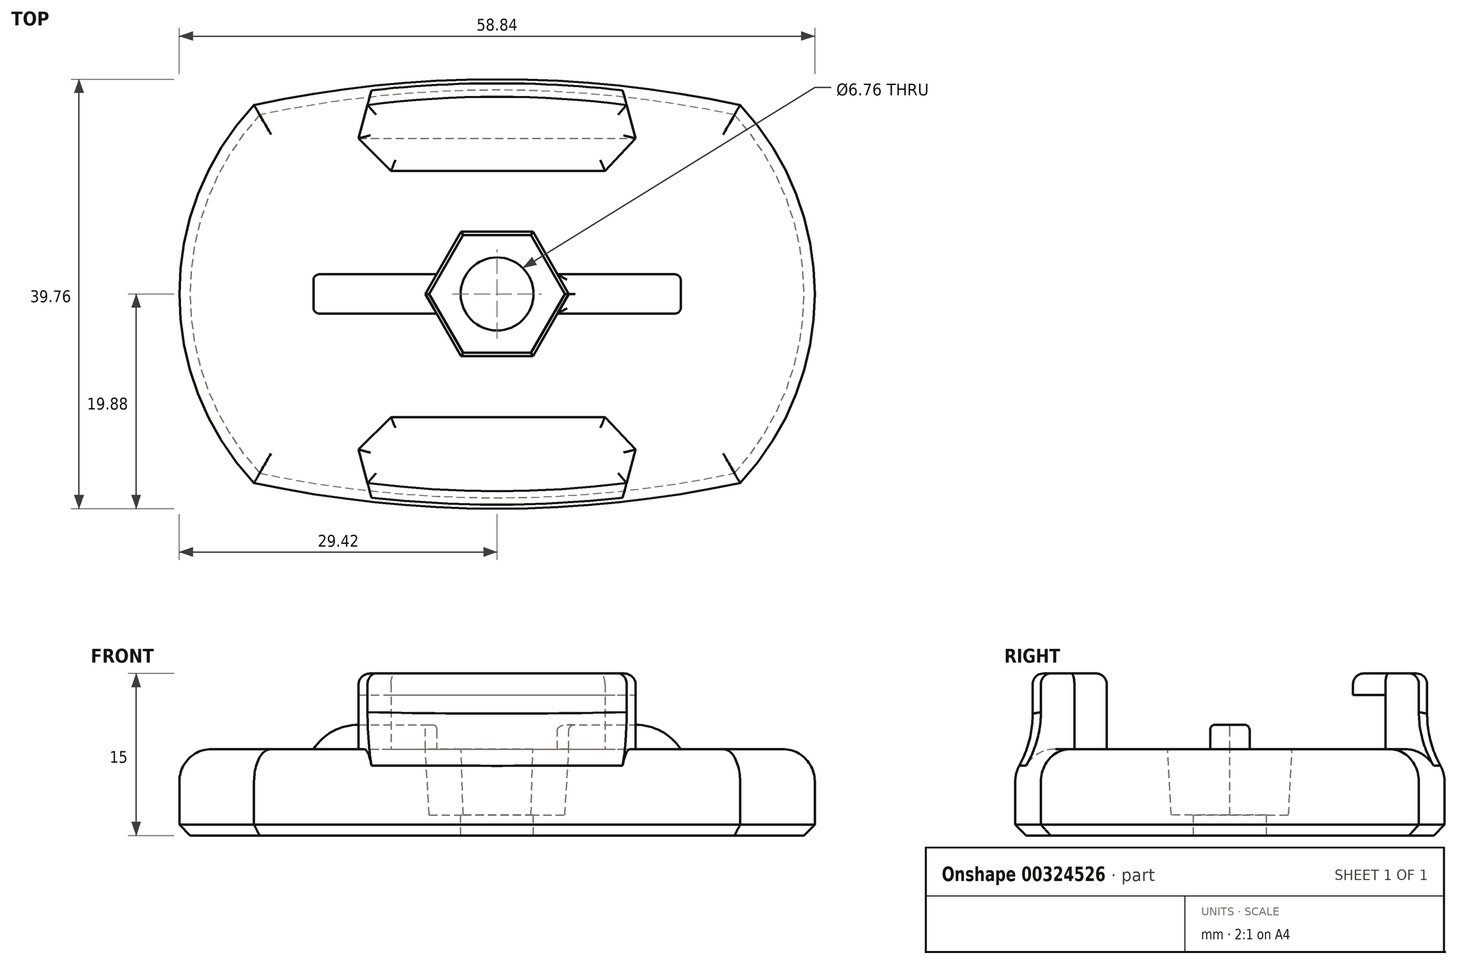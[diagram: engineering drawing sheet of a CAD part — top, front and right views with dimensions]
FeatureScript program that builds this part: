
annotation { "Feature Type Name" : "Feature", "Feature Type Description" : "" }
export const myFeature = defineFeature(function(context is Context, id is Id, definition is map)
    precondition{}
    {
        {
            var Q0;
            Q0=qCreatedBy(makeId("Top.planeOp"),FACE);
            var sketch = newSketch(context, id + "F0", { "sketchPlane" : qUnion([Q0])});
            skLineSegment(sketch, "E0.rect.bottom", {"start": v(-22.5, 17.5) * mm, "end": v(22.5, 17.5) * mm});
            skLineSegment(sketch, "E0.rect.top", {"start": v(-22.5, -17.5) * mm, "end": v(22.5, -17.5) * mm});
            skLineSegment(sketch, "E0.rect.left", {"start": v(-22.5, 17.5) * mm, "end": v(-22.5, -17.5) * mm});
            skLineSegment(sketch, "E0.rect.right", {"start": v(22.5, 17.5) * mm, "end": v(22.5, -17.5) * mm});
            skPoint(sketch, "E0.rect.middle", {"position": v(0, 0) * mm});
            skArc(sketch, "E1", {"start": v(-22.5, 17.5) * mm, "mid": v(-29.42, 0) * mm, "end": v(-22.5, -17.5) * mm});
            skArc(sketch, "E2.MirrorCS", {"start": v(22.5, 17.5) * mm, "mid": v(29.42, 0) * mm, "end": v(22.5, -17.5) * mm});
            skArc(sketch, "E3", {"start": v(22.5, 17.5) * mm, "mid": v(0, 19.88) * mm, "end": v(-22.5, 17.5) * mm});
            skArc(sketch, "E4.MirrorCS", {"start": v(22.5, -17.5) * mm, "mid": v(0, -19.88) * mm, "end": v(-22.5, -17.5) * mm});
            skSolve(sketch);
        }
        {
            var Q0;
            Q0=makeQuery(id+"F0.imprint","IMPRINT",FACE,{"disambiguationData":[TD([[makeQuery(id+"F0.imprint","IMPRINT",EDGE,{"derivedFrom":sQuery(id+"F0.wireOp",EDGE,"E0.rect.bottom")}),-1.0]])]});
            var Q1;
            Q1=makeQuery(id+"F0.imprint","IMPRINT",FACE,{"disambiguationData":[TD([[makeQuery(id+"F0.imprint","IMPRINT",EDGE,{"derivedFrom":sQuery(id+"F0.wireOp",EDGE,"E0.rect.left")}),-1.0]])]});
            var Q2;
            Q2=makeQuery(id+"F0.imprint","IMPRINT",FACE,{"disambiguationData":[TD([[makeQuery(id+"F0.imprint","IMPRINT",EDGE,{"derivedFrom":sQuery(id+"F0.wireOp",EDGE,"E0.rect.right")}),1.0]])]});
            var Q3;
            Q3=makeQuery(id+"F0.imprint","IMPRINT",FACE,{"disambiguationData":[TD([[makeQuery(id+"F0.imprint","IMPRINT",EDGE,{"derivedFrom":sQuery(id+"F0.wireOp",EDGE,"E0.rect.bottom")}),1.0]])]});
            var Q4;
            Q4=makeQuery(id+"F0.imprint","IMPRINT",FACE,{"disambiguationData":[TD([[makeQuery(id+"F0.imprint","IMPRINT",EDGE,{"derivedFrom":sQuery(id+"F0.wireOp",EDGE,"E0.rect.top")}),-1.0]])]});
            extrude(context, id + "F1", {"entities" : qUnion([Q0, Q1, Q2, Q3, Q4]), "depth" : 8 * mm});
        }
        {
            var Q0;
            Q0=makeQuery(id+"F1.opExtrude","CAP_FACE",FACE,{"disambiguationData":[OSD([sQuery(id+"F0.wireOp",EDGE,"E1"),sQuery(id+"F0.wireOp",EDGE,"E2.MirrorCS"),sQuery(id+"F0.wireOp",EDGE,"E3"),sQuery(id+"F0.wireOp",EDGE,"E4.MirrorCS")])],"isStart":false});
            var sketch = newSketch(context, id + "F2", { "sketchPlane" : qUnion([Q0])});
            skLineSegment(sketch, "E5.rect.bottom", {"start": v(-17, 1.82) * mm, "end": v(17, 1.82) * mm});
            skLineSegment(sketch, "E5.rect.top", {"start": v(-17, -1.83) * mm, "end": v(17, -1.83) * mm});
            skLineSegment(sketch, "E5.rect.left", {"start": v(-17, 1.82) * mm, "end": v(-17, -1.83) * mm});
            skLineSegment(sketch, "E5.rect.right", {"start": v(17, 1.82) * mm, "end": v(17, -1.83) * mm});
            skPoint(sketch, "E5.rect.middle", {"position": v(0, 0) * mm});
            skSolve(sketch);
        }
        {
            var Q0;
            Q0=makeQuery(id+"F2.imprint","IMPRINT",FACE,{"disambiguationData":[TD([[makeQuery(id+"F2.imprint","IMPRINT",EDGE,{"derivedFrom":sQuery(id+"F2.wireOp",EDGE,"E5.rect.bottom")}),-1.0]])]});
            extrude(context, id + "F3", {"entities" : qUnion([Q0]), "operationType" : NewBodyOperationType.ADD, "depth" : 2.25 * mm});
        }
        {
            var Q0;
            Q0=makeQuery(id+"F3.opExtrude","SWEPT_FACE",FACE,{"disambiguationData":[OSD([sQuery(id+"F2.wireOp",EDGE,"E5.rect.top")])]});
            var sketch = newSketch(context, id + "F4", { "sketchPlane" : qUnion([Q0])});
            skLineSegment(sketch, "E6", {"start": v(-17, 10.25) * mm, "end": v(17, 10.25) * mm, "construction": true});
            skLineSegment(sketch, "E7.0", {"start": v(-17, 9.25) * mm, "end": v(17, 9.25) * mm});
            skArc(sketch, "E8", {"start": v(-13.26, 10.25) * mm, "mid": v(-15.2, 10) * mm, "end": v(-17, 9.25) * mm});
            skLineSegment(sketch, "E9", {"start": v(0, 0) * mm, "end": v(0, 15.47) * mm, "construction": true});
            skArc(sketch, "E10.0.MirrorCS", {"start": v(13.26, 10.25) * mm, "mid": v(15.2, 10) * mm, "end": v(17, 9.25) * mm});
            skLineSegment(sketch, "E11", {"start": v(-17, 9.25) * mm, "end": v(-18.16, 9.25) * mm});
            skLineSegment(sketch, "E12", {"start": v(-18.16, 9.25) * mm, "end": v(-18.16, 11.7) * mm});
            skLineSegment(sketch, "E13", {"start": v(-18.16, 11.7) * mm, "end": v(-13.25, 11.7) * mm});
            skLineSegment(sketch, "E14", {"start": v(-13.25, 11.7) * mm, "end": v(-13.26, 10.25) * mm});
            skLineSegment(sketch, "E15", {"start": v(13.26, 10.25) * mm, "end": v(13.26, 11.4) * mm});
            skLineSegment(sketch, "E16", {"start": v(13.26, 11.4) * mm, "end": v(18.11, 11.4) * mm});
            skLineSegment(sketch, "E17", {"start": v(18.11, 11.4) * mm, "end": v(18.11, 9.28) * mm});
            skLineSegment(sketch, "E18", {"start": v(18.11, 9.28) * mm, "end": v(17, 9.25) * mm});
            skSolve(sketch);
        }
        {
            var Q0;
            Q0=makeQuery(id+"F1.opExtrude","CAP_FACE",FACE,{"disambiguationData":[OSD([sQuery(id+"F0.wireOp",EDGE,"E1"),sQuery(id+"F0.wireOp",EDGE,"E2.MirrorCS"),sQuery(id+"F0.wireOp",EDGE,"E3"),sQuery(id+"F0.wireOp",EDGE,"E4.MirrorCS")])],"isStart":false});
            var sketch = newSketch(context, id + "F5", { "sketchPlane" : qUnion([Q0])});
            skLineSegment(sketch, "E19.rect.bottom", {"start": v(-12, 17.5) * mm, "end": v(12, 17.5) * mm, "construction": true});
            skPoint(sketch, "E19.rect.middle", {"position": v(0, 0) * mm});
            skLineSegment(sketch, "E20.0", {"start": v(-9.82, 11.4) * mm, "end": v(10, 11.4) * mm});
            skLineSegment(sketch, "E21", {"start": v(-9.82, 11.4) * mm, "end": v(-12.82, 14.4) * mm, "construction": true});
            skLineSegment(sketch, "E22", {"start": v(-9.82, 11.4) * mm, "end": v(-12.83, 14.4) * mm, "construction": true});
            skLineSegment(sketch, "E23.0.MirrorCS", {"start": v(10, 11.4) * mm, "end": v(12.82, 14.4) * mm, "construction": true});
            skLineSegment(sketch, "E24", {"start": v(10, 11.4) * mm, "end": v(12.82, 14.4) * mm});
            skLineSegment(sketch, "E25", {"start": v(12, 17.5) * mm, "end": v(-12, 17.5) * mm});
            skLineSegment(sketch, "E26", {"start": v(-12.83, 14.4) * mm, "end": v(-9.82, 11.4) * mm});
            skLineSegment(sketch, "E27", {"start": v(12.83, 14.4) * mm, "end": v(12, 17.5) * mm});
            skLineSegment(sketch, "E28.0.MirrorCS", {"start": v(-12.83, 14.4) * mm, "end": v(-12, 17.5) * mm});
            skArc(sketch, "E29", {"start": v(12, 17.5) * mm, "mid": v(0, 18.26) * mm, "end": v(-12, 17.5) * mm});
            skLineSegment(sketch, "E30.MirrorCS", {"start": v(12, -17.5) * mm, "end": v(-12, -17.5) * mm});
            skLineSegment(sketch, "E31.MirrorCS", {"start": v(-12.83, -14.4) * mm, "end": v(-9.82, -11.4) * mm});
            skLineSegment(sketch, "E32.MirrorCS", {"start": v(-9.82, -11.4) * mm, "end": v(-12.82, -14.4) * mm, "construction": true});
            skLineSegment(sketch, "E33.MirrorCS", {"start": v(10, -11.4) * mm, "end": v(12.82, -14.4) * mm});
            skLineSegment(sketch, "E34.MirrorCS", {"start": v(-12, -17.5) * mm, "end": v(12, -17.5) * mm, "construction": true});
            skLineSegment(sketch, "E35.MirrorCS", {"start": v(-9.82, -11.4) * mm, "end": v(-12.83, -14.4) * mm, "construction": true});
            skLineSegment(sketch, "E36.MirrorCS", {"start": v(10, -11.4) * mm, "end": v(12.82, -14.4) * mm, "construction": true});
            skLineSegment(sketch, "E37.MirrorCS", {"start": v(-12.83, -14.4) * mm, "end": v(-12, -17.5) * mm});
            skLineSegment(sketch, "E38.MirrorCS", {"start": v(12.83, -14.4) * mm, "end": v(12, -17.5) * mm});
            skLineSegment(sketch, "E39.MirrorCS", {"start": v(-9.82, -11.4) * mm, "end": v(10, -11.4) * mm});
            skArc(sketch, "E40.MirrorCS", {"start": v(12, -17.5) * mm, "mid": v(0, -18.26) * mm, "end": v(-12, -17.5) * mm});
            skSolve(sketch);
        }
        {
            var Q0;
            Q0 = qSketchRegion(id + "F5", true);
            extrude(context, id + "F6", {"entities" : qUnion([Q0]), "operationType" : NewBodyOperationType.ADD, "depth" : 7 * mm});
        }
        {
            var Q0;
            Q0=qCreatedBy(makeId("Right.planeOp"),FACE);
            var sketch = newSketch(context, id + "F7", { "sketchPlane" : qUnion([Q0])});
            skLineSegment(sketch, "E41.0", {"start": v(14.4, 13) * mm, "end": v(14.4, 8) * mm});
            skLineSegment(sketch, "E42.bottom", {"start": v(14.4, 8) * mm, "end": v(10.15, 8) * mm});
            skLineSegment(sketch, "E42.top", {"start": v(14.4, 13) * mm, "end": v(10.15, 13) * mm});
            skLineSegment(sketch, "E42.left", {"start": v(14.4, 8) * mm, "end": v(14.4, 13) * mm});
            skLineSegment(sketch, "E42.right", {"start": v(10.15, 8) * mm, "end": v(10.15, 13) * mm});
            skLineSegment(sketch, "E43.0.MirrorCS", {"start": v(-14.4, 8) * mm, "end": v(-14.4, 13) * mm});
            skLineSegment(sketch, "E43.1.MirrorCS", {"start": v(-14.4, 13) * mm, "end": v(-14.4, 8) * mm});
            skLineSegment(sketch, "E43.2.MirrorCS", {"start": v(-14.4, 13) * mm, "end": v(-10.15, 13) * mm});
            skLineSegment(sketch, "E43.3.MirrorCS", {"start": v(-10.15, 8) * mm, "end": v(-10.15, 13) * mm});
            skLineSegment(sketch, "E43.4.MirrorCS", {"start": v(-14.4, 8) * mm, "end": v(-10.15, 8) * mm});
            skSolve(sketch);
        }
        {
            var Q0;
            Q0=makeQuery(id+"F7.imprint","IMPRINT",FACE,{"disambiguationData":[TD([[makeQuery(id+"F7.imprint","IMPRINT",EDGE,{"derivedFrom":sQuery(id+"F7.wireOp",EDGE,"E42.bottom")}),-1.0]])]});
            var Q1;
            Q1=makeQuery(id+"F7.imprint","IMPRINT",FACE,{"disambiguationData":[TD([[makeQuery(id+"F7.imprint","IMPRINT",EDGE,{"derivedFrom":sQuery(id+"F7.wireOp",EDGE,"E43.1.MirrorCS")}),1.0]])]});
            extrude(context, id + "F8", {"entities" : qUnion([Q0, Q1]), "operationType" : NewBodyOperationType.REMOVE, "endBound" : BoundingType.SYMMETRIC, "oppositeDirection" : true, "depth" : 31.01 * mm});
        }
        {
            var Q0;
            Q0=makeQuery(id+"F1.opExtrude","CAP_EDGE",EDGE,{"disambiguationData":[OSD([sQuery(id+"F0.wireOp",EDGE,"E3")])],"isStart":false});
            var Q1;
            Q1=makeQuery(id+"F1.opExtrude","CAP_EDGE",EDGE,{"disambiguationData":[OSD([sQuery(id+"F0.wireOp",EDGE,"E1")])],"isStart":false});
            var Q2;
            Q2=makeQuery(id+"F1.opExtrude","CAP_EDGE",EDGE,{"disambiguationData":[OSD([sQuery(id+"F0.wireOp",EDGE,"E4.MirrorCS")])],"isStart":false});
            var Q3;
            Q3=makeQuery(id+"F1.opExtrude","CAP_EDGE",EDGE,{"disambiguationData":[OSD([sQuery(id+"F0.wireOp",EDGE,"E2.MirrorCS")])],"isStart":false});
            fillet(context, id + "F9", {"entities" : qUnion([Q0, Q1, Q2, Q3]), "radius" : 3 * mm, "tangentPropagation" : true, "allowEdgeOverflow" : false});
        }
        {
            var Q0;
            Q0=makeQuery(id+"F9.opFillet","BLEND_EDGE",EDGE,{"blendedFrom":[makeQuery(id+"F1.opExtrude","CAP_EDGE",EDGE,{"disambiguationData":[OSD([sQuery(id+"F0.wireOp",EDGE,"E4.MirrorCS")])],"isStart":false}),makeQuery(id+"F6.opExtrude","SWEPT_FACE",FACE,{"disambiguationData":[OSD([sQuery(id+"F5.wireOp",EDGE,"E40.MirrorCS")])]})],"blendedInto":[makeQuery(id+"F6.opExtrude","SWEPT_FACE",FACE,{"disambiguationData":[OSD([sQuery(id+"F5.wireOp",EDGE,"E40.MirrorCS")])]})]});
            var Q1;
            Q1=makeQuery(id+"F9.opFillet","BLEND_EDGE",EDGE,{"blendedFrom":[makeQuery(id+"F1.opExtrude","CAP_EDGE",EDGE,{"disambiguationData":[OSD([sQuery(id+"F0.wireOp",EDGE,"E3")])],"isStart":false}),makeQuery(id+"F6.opExtrude","SWEPT_FACE",FACE,{"disambiguationData":[OSD([sQuery(id+"F5.wireOp",EDGE,"E29")])]})],"blendedInto":[makeQuery(id+"F6.opExtrude","SWEPT_FACE",FACE,{"disambiguationData":[OSD([sQuery(id+"F5.wireOp",EDGE,"E29")])]})]});
            fillet(context, id + "F10", {"entities" : qUnion([Q0, Q1]), "radius" : 10 * mm, "tangentPropagation" : true, "allowEdgeOverflow" : false});
        }
        {
            var Q0;
            Q0=makeQuery(id+"F6.opExtrude","CAP_FACE",FACE,{"disambiguationData":[OSD([sQuery(id+"F5.wireOp",EDGE,"E31.MirrorCS"),sQuery(id+"F5.wireOp",EDGE,"E33.MirrorCS"),sQuery(id+"F5.wireOp",EDGE,"E37.MirrorCS"),sQuery(id+"F5.wireOp",EDGE,"E38.MirrorCS"),sQuery(id+"F5.wireOp",EDGE,"E39.MirrorCS"),sQuery(id+"F5.wireOp",EDGE,"E40.MirrorCS")])],"isStart":false});
            var Q1;
            Q1=makeQuery(id+"F6.opExtrude","CAP_FACE",FACE,{"disambiguationData":[OSD([sQuery(id+"F5.wireOp",EDGE,"E20.0"),sQuery(id+"F5.wireOp",EDGE,"E24"),sQuery(id+"F5.wireOp",EDGE,"E26"),sQuery(id+"F5.wireOp",EDGE,"E27"),sQuery(id+"F5.wireOp",EDGE,"E28.0.MirrorCS"),sQuery(id+"F5.wireOp",EDGE,"E29")])],"isStart":false});
            fillet(context, id + "F11", {"entities" : qUnion([Q0, Q1]), "radius" : 1 * mm, "tangentPropagation" : true, "allowEdgeOverflow" : false});
        }
        {
            var Q0;
            Q0=makeQuery(id+"F8.boolean.opBoolean","MERGE",FACE,{"derivedFrom":[makeQuery(id+"F1.opExtrude","CAP_FACE",FACE,{"disambiguationData":[OSD([sQuery(id+"F0.wireOp",EDGE,"E0.rect.bottom"),sQuery(id+"F0.wireOp",EDGE,"E0.rect.top"),sQuery(id+"F0.wireOp",EDGE,"E1"),sQuery(id+"F0.wireOp",EDGE,"E2.MirrorCS")])],"isStart":false}),makeQuery(id+"F8.opExtrude","SWEPT_FACE",FACE,{"disambiguationData":[OSD([sQuery(id+"F7.wireOp",EDGE,"E42.bottom")])]}),makeQuery(id+"F8.opExtrude","SWEPT_FACE",FACE,{"disambiguationData":[OSD([sQuery(id+"F7.wireOp",EDGE,"E43.4.MirrorCS")])]})]});
            var sketch = newSketch(context, id + "F12", { "sketchPlane" : qUnion([Q0])});
            skCircle(sketch, "E44.cCircle", {"center": v(0, 0) * mm, "radius": 5.76 * mm, "construction": true});
            skLineSegment(sketch, "E44.0", {"start": v(-3.32, -5.76) * mm, "end": v(-6.65, 0) * mm});
            skLineSegment(sketch, "E44.1", {"start": v(-6.65, 0) * mm, "end": v(-3.32, 5.76) * mm});
            skLineSegment(sketch, "E44.2", {"start": v(-3.32, 5.76) * mm, "end": v(3.32, 5.76) * mm});
            skLineSegment(sketch, "E44.3", {"start": v(3.32, 5.76) * mm, "end": v(6.65, 0) * mm});
            skLineSegment(sketch, "E44.4", {"start": v(6.65, 0) * mm, "end": v(3.32, -5.76) * mm});
            skLineSegment(sketch, "E44.5", {"start": v(3.32, -5.76) * mm, "end": v(-3.32, -5.76) * mm});
            skPoint(sketch, "E44.0.midPoint", {"position": v(-4.99, -2.88) * mm});
            skSolve(sketch);
        }
        {
            var Q0;
            Q0 = qSketchRegion(id + "F12", true);
            var Q1;
            Q1=makeQuery(id+"F3.opExtrude","CAP_FACE",FACE,{"disambiguationData":[OSD([sQuery(id+"F2.wireOp",EDGE,"E5.rect.bottom"),sQuery(id+"F2.wireOp",EDGE,"E5.rect.top"),sQuery(id+"F2.wireOp",EDGE,"E5.rect.left"),sQuery(id+"F2.wireOp",EDGE,"E5.rect.right")])],"isStart":false});
            extrude(context, id + "F13", {"entities" : qUnion([Q0]), "operationType" : NewBodyOperationType.REMOVE, "oppositeDirection" : true, "depth" : (7 / 32) * 27.94 * mm, "hasDraft" : true, "draftAngle" : 3 * degree, "draftPullDirection" : true, "hasSecondDirection" : true, "secondDirectionBound" : SecondDirectionBoundingType.UP_TO_SURFACE, "secondDirectionOppositeDirection" : false, "secondDirectionBoundEntityFace" : qUnion([Q1]), "secondDirectionDepth" : 25 * mm});
        }
        {
            var Q0;
            Q0=sQuery(id+"F12.wireOp",VERTEX,"E44.cCircle.center");
            var Q1;
            Q1=makeQuery(id+"F1.opExtrude","SWEPT_BODY",BODY,{"disambiguationData":[OSD([sQuery(id+"F0.wireOp",EDGE,"E0.rect.bottom"),sQuery(id+"F0.wireOp",EDGE,"E0.rect.top"),sQuery(id+"F0.wireOp",EDGE,"E1"),sQuery(id+"F0.wireOp",EDGE,"E2.MirrorCS")])]});
            hole(context, id + "F14", {"style" : HoleStyle.SIMPLE, "endStyle" : HoleEndStyle.THROUGH, "standardTappedOrClearance" : lookupTablePath({ "standard" : "ANSI", "fit" : "Normal (ASME)", "size" : "1/4", "type" : "Clearance" }), "standardBlindInLast" : lookupTablePath({ "fit" : "Free", "standard" : "ANSI", "size" : "1/4", "type" : "Clearance" }), "holeDiameter" : 6.76 * mm, "tappedDepth" : 12 * mm, "tapClearance" : 3, "locations" : qUnion([Q0]), "scope" : qUnion([Q1])});
        }
        {
            var Q0;
            Q0=makeQuery(id+"F1.opExtrude","CAP_EDGE",EDGE,{"disambiguationData":[OSD([sQuery(id+"F0.wireOp",EDGE,"E0.rect.top")])],"isStart":true});
            var Q1;
            Q1=makeQuery(id+"F1.opExtrude","CAP_EDGE",EDGE,{"disambiguationData":[OSD([sQuery(id+"F0.wireOp",EDGE,"E2.MirrorCS")])],"isStart":true});
            var Q2;
            Q2=makeQuery(id+"F1.opExtrude","CAP_EDGE",EDGE,{"disambiguationData":[OSD([sQuery(id+"F0.wireOp",EDGE,"E0.rect.bottom")])],"isStart":true});
            var Q3;
            Q3=makeQuery(id+"F1.opExtrude","CAP_EDGE",EDGE,{"disambiguationData":[OSD([sQuery(id+"F0.wireOp",EDGE,"E1")])],"isStart":true});
            var Q4;
            Q4=makeQuery(id+"F1.opExtrude","CAP_EDGE",EDGE,{"disambiguationData":[OSD([sQuery(id+"F0.wireOp",EDGE,"E3")])],"isStart":true});
            var Q5;
            Q5=makeQuery(id+"F1.opExtrude","CAP_EDGE",EDGE,{"disambiguationData":[OSD([sQuery(id+"F0.wireOp",EDGE,"E4.MirrorCS")])],"isStart":true});
            chamfer(context, id + "F15", {"entities" : qUnion([Q0, Q1, Q2, Q3, Q4, Q5]), "width" : 1 * mm, "tangentPropagation" : true});
        }
        {
            var Q0;
            Q0=makeQuery(id+"F3.opExtrude","CAP_EDGE",EDGE,{"disambiguationData":[OSD([sQuery(id+"F2.wireOp",EDGE,"E5.rect.right")])],"isStart":false});
            var Q1;
            Q1=makeQuery(id+"F3.opExtrude","CAP_EDGE",EDGE,{"disambiguationData":[OSD([sQuery(id+"F2.wireOp",EDGE,"E5.rect.left")])],"isStart":false});
            fillet(context, id + "F16", {"entities" : qUnion([Q0, Q1]), "radius" : 5 * mm, "tangentPropagation" : true, "allowEdgeOverflow" : false});
        }
        {
            var Q0;
            {var subQ0=sQuery(id+"F2.wireOp",EDGE,"E5.rect.right");var subQ1=sQuery(id+"F2.wireOp",EDGE,"E5.rect.top");Q0=makeQuery(id+"F13.boolean.opBoolean","SPLIT",EDGE,{"disambiguationData":[TD([makeQuery(id+"F3.opExtrude","SWEPT_FACE",FACE,{"disambiguationData":[OSD([subQ0])]})])],"derivedFrom":makeQuery(id+"F3.opExtrude","CAP_EDGE",EDGE,{"disambiguationData":[OSD([subQ1])],"isStart":false})});}
            var Q1;
            {var subQ0=sQuery(id+"F2.wireOp",EDGE,"E5.rect.bottom");var subQ1=sQuery(id+"F2.wireOp",EDGE,"E5.rect.right");Q1=makeQuery(id+"F13.boolean.opBoolean","SPLIT",EDGE,{"disambiguationData":[TD([makeQuery(id+"F3.opExtrude","SWEPT_FACE",FACE,{"disambiguationData":[OSD([subQ1])]})])],"derivedFrom":makeQuery(id+"F3.opExtrude","CAP_EDGE",EDGE,{"disambiguationData":[OSD([subQ0])],"isStart":false})});}
            var Q2;
            {var subQ0=sQuery(id+"F2.wireOp",EDGE,"E5.rect.bottom");var subQ1=sQuery(id+"F2.wireOp",EDGE,"E5.rect.left");Q2=makeQuery(id+"F13.boolean.opBoolean","SPLIT",EDGE,{"disambiguationData":[TD([makeQuery(id+"F3.opExtrude","SWEPT_FACE",FACE,{"disambiguationData":[OSD([subQ1])]})])],"derivedFrom":makeQuery(id+"F3.opExtrude","CAP_EDGE",EDGE,{"disambiguationData":[OSD([subQ0])],"isStart":false})});}
            var Q3;
            {var subQ0=sQuery(id+"F2.wireOp",EDGE,"E5.rect.left");var subQ1=sQuery(id+"F2.wireOp",EDGE,"E5.rect.top");Q3=makeQuery(id+"F13.boolean.opBoolean","SPLIT",EDGE,{"disambiguationData":[TD([makeQuery(id+"F3.opExtrude","SWEPT_FACE",FACE,{"disambiguationData":[OSD([subQ0])]})])],"derivedFrom":makeQuery(id+"F3.opExtrude","CAP_EDGE",EDGE,{"disambiguationData":[OSD([subQ1])],"isStart":false})});}
            var Q4;
            Q4=makeQuery(id+"F13.boolean.opBoolean","COPY",EDGE,{"derivedFrom":makeQuery(id+"F13.opExtrude","CAP_EDGE",EDGE,{"disambiguationData":[OSD([sQuery(id+"F12.wireOp",EDGE,"E44.1")])],"isStart":true})});
            var Q5;
            Q5=makeQuery(id+"F13.boolean.opBoolean","COPY",EDGE,{"derivedFrom":makeQuery(id+"F13.opExtrude","CAP_EDGE",EDGE,{"disambiguationData":[OSD([sQuery(id+"F12.wireOp",EDGE,"E44.0")])],"isStart":true})});
            var Q6;
            Q6=makeQuery(id+"F13.boolean.opBoolean","COPY",EDGE,{"derivedFrom":makeQuery(id+"F13.opExtrude","CAP_EDGE",EDGE,{"disambiguationData":[OSD([sQuery(id+"F12.wireOp",EDGE,"E44.4")])],"isStart":true})});
            var Q7;
            Q7=makeQuery(id+"F13.boolean.opBoolean","COPY",EDGE,{"derivedFrom":makeQuery(id+"F13.opExtrude","CAP_EDGE",EDGE,{"disambiguationData":[OSD([sQuery(id+"F12.wireOp",EDGE,"E44.3")])],"isStart":true})});
            fillet(context, id + "F17", {"entities" : qUnion([Q0, Q1, Q2, Q3, Q4, Q5, Q6, Q7]), "radius" : .5 * mm, "tangentPropagation" : true, "allowEdgeOverflow" : false});
        }
    });
